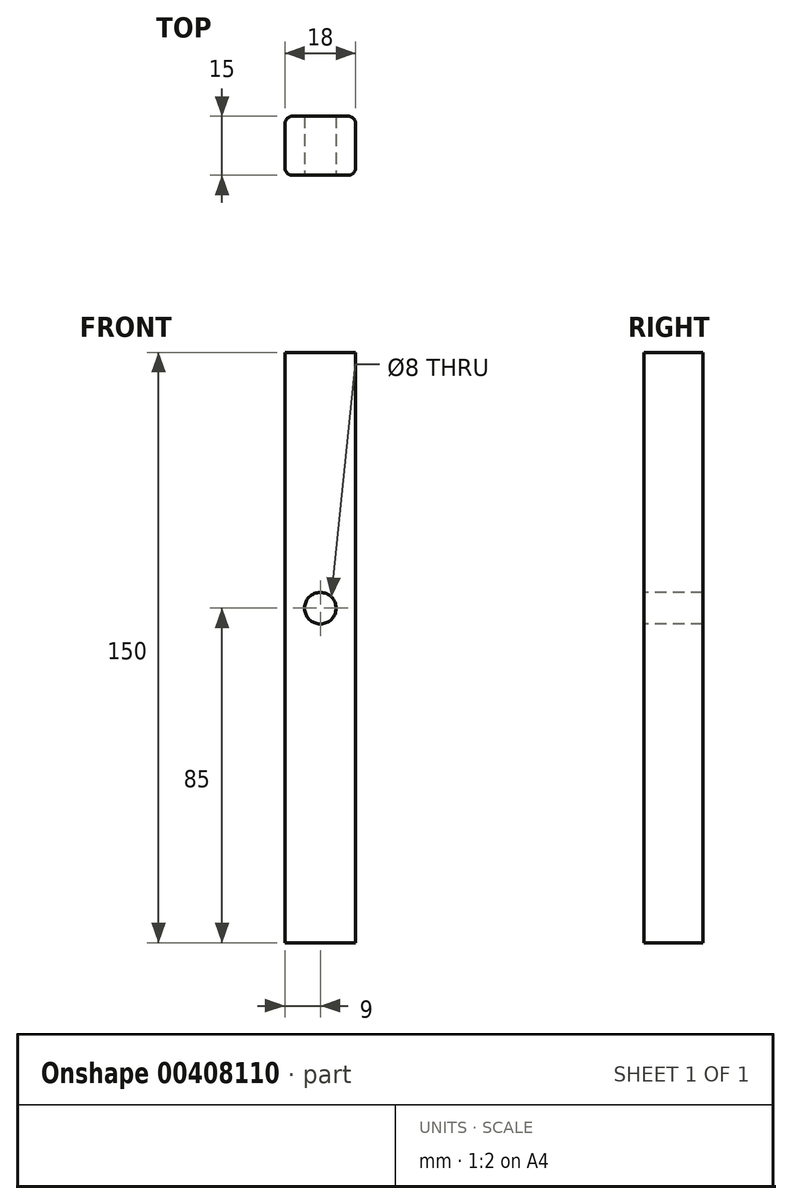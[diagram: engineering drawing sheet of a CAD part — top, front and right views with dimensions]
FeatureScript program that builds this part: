
annotation { "Feature Type Name" : "Feature", "Feature Type Description" : "" }
export const myFeature = defineFeature(function(context is Context, id is Id, definition is map)
    precondition{}
    {
        {
            var Q0;
            Q0=qCreatedBy(makeId("Front.planeOp"),FACE);
            var sketch = newSketch(context, id + "F0", { "sketchPlane" : qUnion([Q0])});
            skLineSegment(sketch, "E0.bottom", {"start": v(9, 75) * mm, "end": v(-9, 75) * mm});
            skLineSegment(sketch, "E0.top", {"start": v(9, -75) * mm, "end": v(-9, -75) * mm});
            skLineSegment(sketch, "E0.left", {"start": v(9, 75) * mm, "end": v(9, -75) * mm});
            skLineSegment(sketch, "E0.right", {"start": v(-9, 75) * mm, "end": v(-9, -75) * mm});
            skPoint(sketch, "E0.middle", {"position": v(0, 0) * mm});
            skSolve(sketch);
        }
        {
            var Q0;
            Q0 = qSketchRegion(id + "F0", true);
            extrude(context, id + "F1", {"entities" : qUnion([Q0]), "endBound" : BoundingType.SYMMETRIC, "depth" : 15 * mm});
        }
        {
            var Q0;
            Q0=makeQuery(id+"F1.opExtrude","CAP_EDGE",EDGE,{"disambiguationData":[OSD([sQuery(id+"F0.wireOp",EDGE,"E0.right")])],"isStart":false});
            var Q1;
            Q1=makeQuery(id+"F1.opExtrude","CAP_EDGE",EDGE,{"disambiguationData":[OSD([sQuery(id+"F0.wireOp",EDGE,"E0.left")])],"isStart":false});
            var Q2;
            Q2=makeQuery(id+"F1.opExtrude","CAP_EDGE",EDGE,{"disambiguationData":[OSD([sQuery(id+"F0.wireOp",EDGE,"E0.left")])],"isStart":true});
            var Q3;
            Q3=makeQuery(id+"F1.opExtrude","CAP_EDGE",EDGE,{"disambiguationData":[OSD([sQuery(id+"F0.wireOp",EDGE,"E0.right")])],"isStart":true});
            fillet(context, id + "F2", {"entities" : qUnion([Q0, Q1, Q2, Q3]), "radius" : 2 * mm, "tangentPropagation" : true, "allowEdgeOverflow" : false});
        }
        {
            var Q0;
            Q0=makeQuery(id+"F1.opExtrude","CAP_FACE",FACE,{"disambiguationData":[OSD([sQuery(id+"F0.wireOp",EDGE,"E0.bottom"),sQuery(id+"F0.wireOp",EDGE,"E0.top"),sQuery(id+"F0.wireOp",EDGE,"E0.left"),sQuery(id+"F0.wireOp",EDGE,"E0.right")])],"isStart":false});
            var sketch = newSketch(context, id + "F3", { "sketchPlane" : qUnion([Q0])});
            skCircle(sketch, "E1", {"center": v(0, 10) * mm, "radius": 4 * mm});
            skSolve(sketch);
        }
        {
            var Q0;
            Q0 = qSketchRegion(id + "F3", true);
            extrude(context, id + "F4", {"entities" : qUnion([Q0]), "operationType" : NewBodyOperationType.REMOVE, "oppositeDirection" : true, "depth" : 25.4 * mm});
        }
    });
